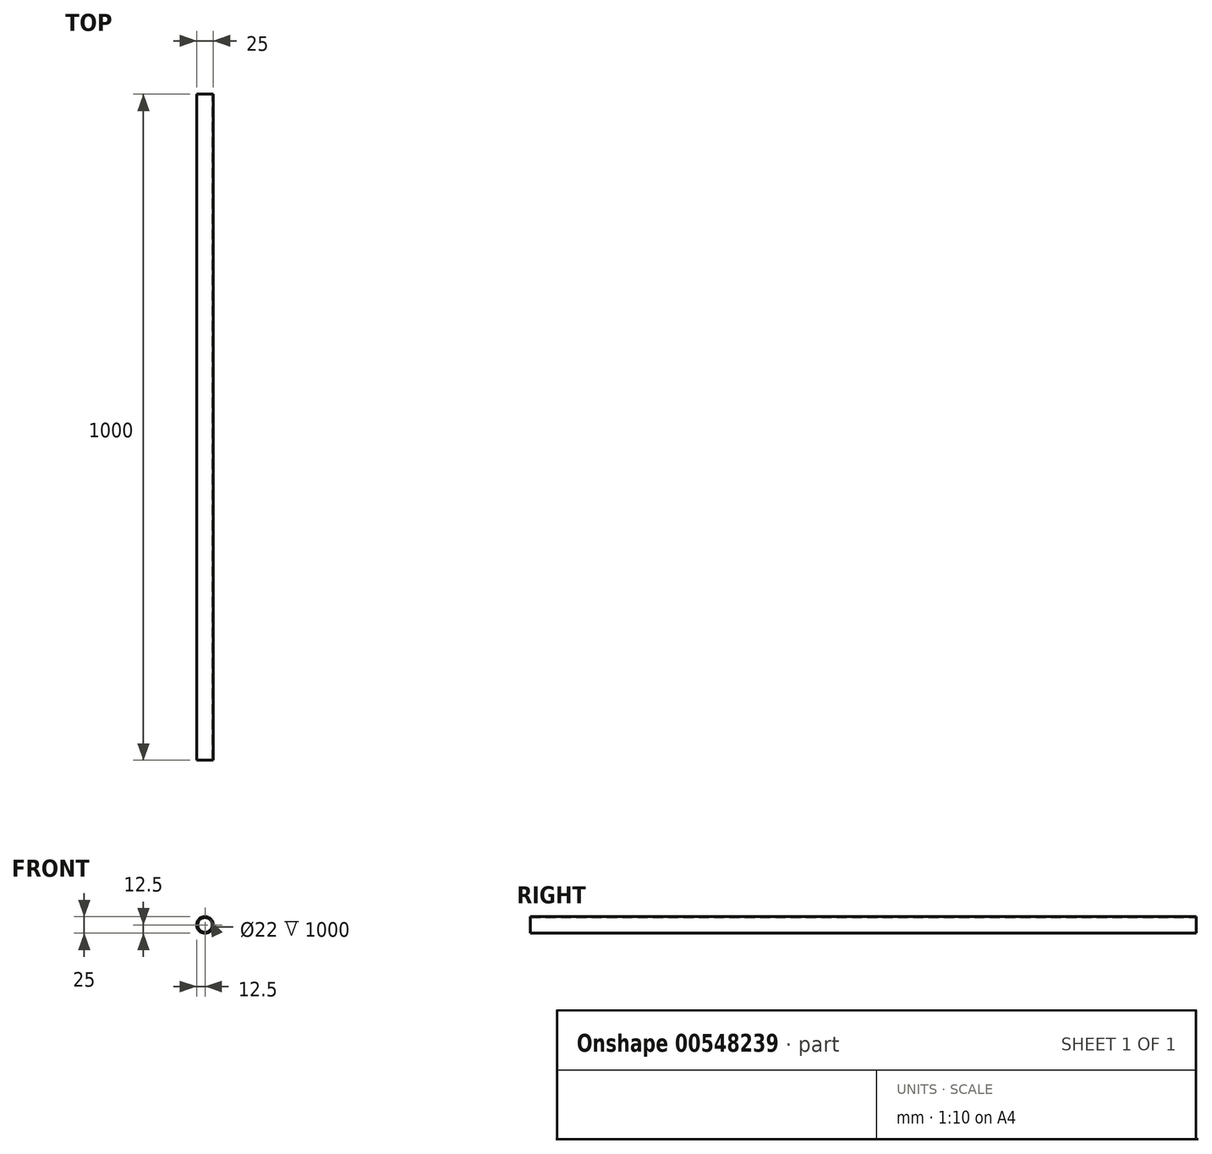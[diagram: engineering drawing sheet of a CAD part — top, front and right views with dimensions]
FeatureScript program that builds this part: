
annotation { "Feature Type Name" : "Feature", "Feature Type Description" : "" }
export const myFeature = defineFeature(function(context is Context, id is Id, definition is map)
    precondition{}
    {
        {
            var Q0;
            Q0=qCreatedBy(makeId("Front.planeOp"),FACE);
            var sketch = newSketch(context, id + "F0", { "sketchPlane" : qUnion([Q0])});
            skCircle(sketch, "E0", {"center": v(0, 0) * mm, "radius": 12.5 * mm});
            skCircle(sketch, "E1.0", {"center": v(0, 0) * mm, "radius": 11 * mm});
            skSolve(sketch);
        }
        {
            var Q0;
            Q0=makeQuery(id+"F0.imprint","IMPRINT",FACE,{"disambiguationData":[TD([[makeQuery(id+"F0.imprint","IMPRINT",EDGE,{"derivedFrom":sQuery(id+"F0.wireOp",EDGE,"E0")}),1.0]])]});
            extrude(context, id + "F1", {"entities" : qUnion([Q0]), "depth" : 1000 * mm, "offsetDistance" : 25 * mm, "symmetric" : true});
        }
    });
